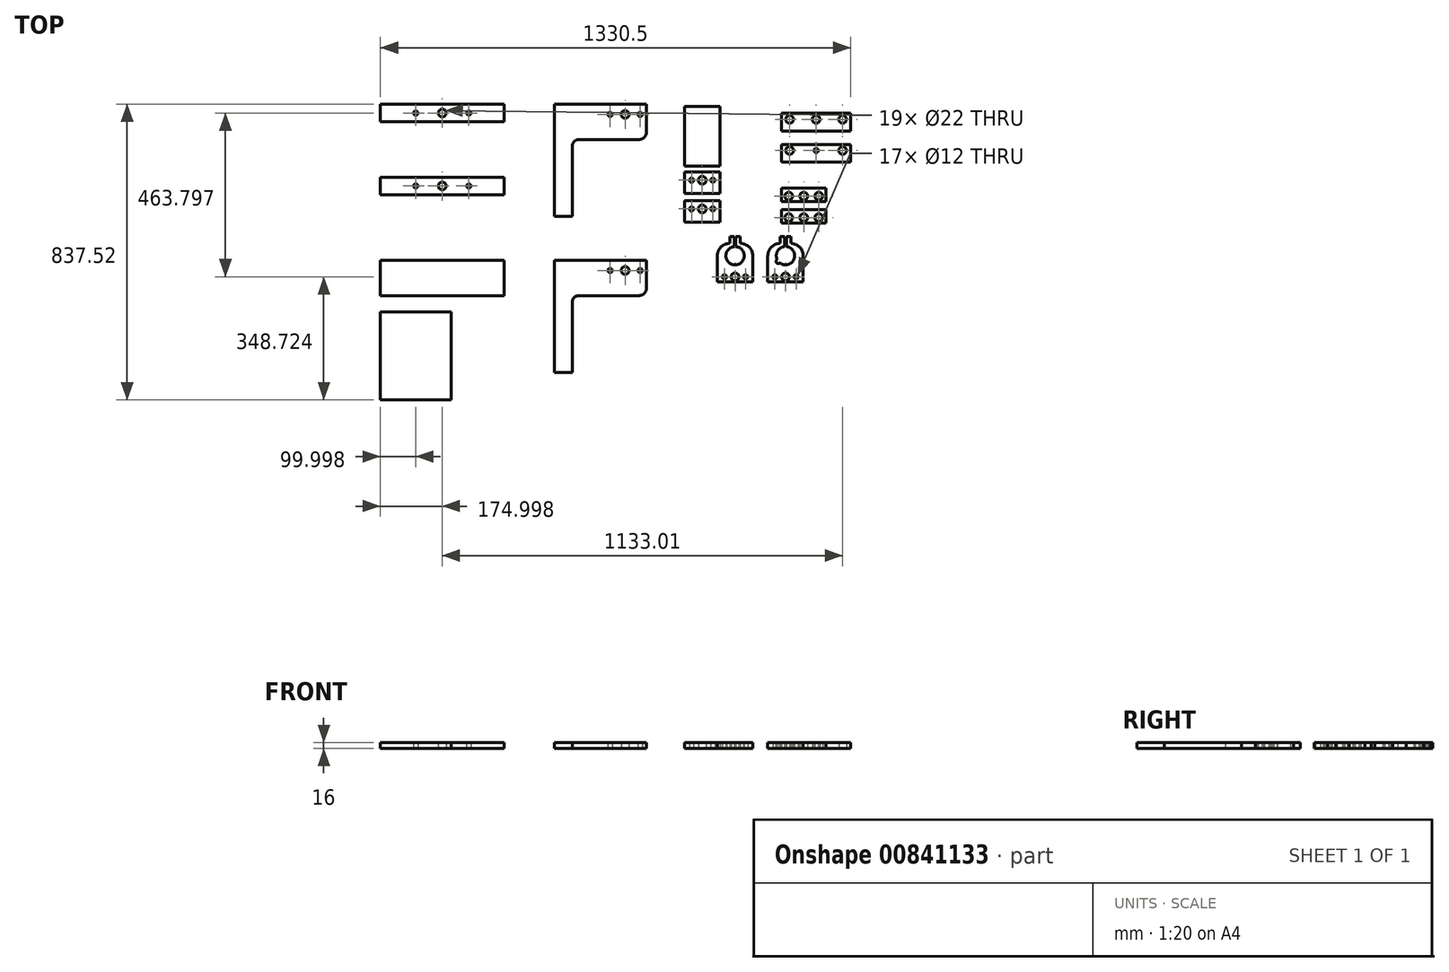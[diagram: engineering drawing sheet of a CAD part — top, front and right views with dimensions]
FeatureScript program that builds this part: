
annotation { "Feature Type Name" : "Feature", "Feature Type Description" : "" }
export const myFeature = defineFeature(function(context is Context, id is Id, definition is map)
    precondition{}
    {
        {
            var Q0;
            Q0=qCreatedBy(makeId("Top.planeOp"),FACE);
            var sketch = newSketch(context, id + "F0", { "sketchPlane" : qUnion([Q0])});
            skLineSegment(sketch, "E0.bottom", {"start": v(-793.1, 335.3) * mm, "end": v(-443.1, 335.3) * mm});
            skLineSegment(sketch, "E0.top", {"start": v(-793.1, 285.3) * mm, "end": v(-443.1, 285.3) * mm});
            skLineSegment(sketch, "E0.left", {"start": v(-793.1, 335.3) * mm, "end": v(-793.1, 285.3) * mm});
            skLineSegment(sketch, "E0.right", {"start": v(-443.1, 335.3) * mm, "end": v(-443.1, 285.3) * mm});
            skLineSegment(sketch, "E1.bottom", {"start": v(-793.1, 100) * mm, "end": v(-443.1, 100) * mm});
            skLineSegment(sketch, "E1.top", {"start": v(-793.1, 0) * mm, "end": v(-443.1, 0) * mm});
            skLineSegment(sketch, "E1.left", {"start": v(-793.1, 100) * mm, "end": v(-793.1, 0) * mm});
            skLineSegment(sketch, "E1.right", {"start": v(-443.1, 100) * mm, "end": v(-443.1, 0) * mm});
            skLineSegment(sketch, "E2", {"start": v(-300.58, 541.75) * mm, "end": v(-40.58, 541.75) * mm});
            skLineSegment(sketch, "E3", {"start": v(-40.58, 541.75) * mm, "end": v(-40.58, 461.75) * mm});
            skLineSegment(sketch, "E4", {"start": v(-60.58, 441.75) * mm, "end": v(-230.58, 441.75) * mm});
            skLineSegment(sketch, "E5", {"start": v(-250.58, 421.75) * mm, "end": v(-250.58, 223.75) * mm});
            skLineSegment(sketch, "E6", {"start": v(-250.58, 223.75) * mm, "end": v(-300.58, 223.75) * mm});
            skLineSegment(sketch, "E7", {"start": v(-300.58, 223.75) * mm, "end": v(-300.58, 541.75) * mm});
            skCircle(sketch, "E8", {"center": v(-693.1, 310.3) * mm, "radius": 6 * mm});
            skCircle(sketch, "E9", {"center": v(-543.1, 310.3) * mm, "radius": 6 * mm});
            skLineSegment(sketch, "E10", {"start": v(-793.1, 310.3) * mm, "end": v(-443.1, 310.3) * mm, "construction": true});
            skCircle(sketch, "E11", {"center": v(-618.1, 310.3) * mm, "radius": 11 * mm});
            skLineSegment(sketch, "E12.bottom", {"start": v(-793.1, 541.75) * mm, "end": v(-443.1, 541.75) * mm});
            skLineSegment(sketch, "E12.top", {"start": v(-793.1, 491.75) * mm, "end": v(-443.1, 491.75) * mm});
            skLineSegment(sketch, "E12.left", {"start": v(-793.1, 541.75) * mm, "end": v(-793.1, 491.75) * mm});
            skLineSegment(sketch, "E12.right", {"start": v(-443.1, 541.75) * mm, "end": v(-443.1, 491.75) * mm});
            skLineSegment(sketch, "E13", {"start": v(-793.1, 516.75) * mm, "end": v(-443.1, 516.75) * mm, "construction": true});
            skCircle(sketch, "E14", {"center": v(-693.1, 516.75) * mm, "radius": 6 * mm});
            skCircle(sketch, "E15", {"center": v(-543.1, 516.75) * mm, "radius": 6 * mm});
            skCircle(sketch, "E16", {"center": v(-618.1, 516.75) * mm, "radius": 11 * mm});
            skLineSegment(sketch, "E17", {"start": v(-300.58, 100) * mm, "end": v(-40.58, 100) * mm});
            skLineSegment(sketch, "E18", {"start": v(-40.58, 100) * mm, "end": v(-40.58, 20) * mm});
            skLineSegment(sketch, "E19", {"start": v(-60.58, 0) * mm, "end": v(-230.58, 0) * mm});
            skLineSegment(sketch, "E20", {"start": v(-250.58, -20) * mm, "end": v(-250.58, -218) * mm});
            skLineSegment(sketch, "E21", {"start": v(-250.58, -218) * mm, "end": v(-300.58, -218) * mm});
            skLineSegment(sketch, "E22", {"start": v(-300.58, -218) * mm, "end": v(-300.58, 100) * mm});
            skLineSegment(sketch, "E23", {"start": v(-40.58, 512.75) * mm, "end": v(-300.58, 512.75) * mm, "construction": true});
            skLineSegment(sketch, "E24", {"start": v(-40.58, 71) * mm, "end": v(-300.58, 71) * mm, "construction": true});
            skCircle(sketch, "E25", {"center": v(-58.15, 512.75) * mm, "radius": 6 * mm});
            skCircle(sketch, "E26", {"center": v(-143.15, 512.75) * mm, "radius": 6 * mm});
            skCircle(sketch, "E27", {"center": v(-58.15, 71) * mm, "radius": 6 * mm});
            skCircle(sketch, "E28", {"center": v(-143.15, 71) * mm, "radius": 6 * mm});
            skCircle(sketch, "E29", {"center": v(-100.58, 512.75) * mm, "radius": 11 * mm});
            skCircle(sketch, "E30", {"center": v(-100.58, 71) * mm, "radius": 11 * mm});
            skPoint(sketch, "E31.visualSharp", {"position": v(-40.58, 441.75) * mm});
            skArc(sketch, "E31.filletArc", {"start": v(-60.58, 441.75) * mm, "mid": v(-46.44, 447.6) * mm, "end": v(-40.58, 461.75) * mm});
            skPoint(sketch, "E32.visualSharp", {"position": v(-250.58, 441.75) * mm});
            skArc(sketch, "E32.filletArc", {"start": v(-230.58, 441.75) * mm, "mid": v(-244.73, 435.9) * mm, "end": v(-250.58, 421.75) * mm});
            skPoint(sketch, "E33.visualSharp", {"position": v(-40.58, 0) * mm});
            skArc(sketch, "E33.filletArc", {"start": v(-60.58, 0) * mm, "mid": v(-46.44, 5.86) * mm, "end": v(-40.58, 20) * mm});
            skPoint(sketch, "E34.visualSharp", {"position": v(-250.58, 0) * mm});
            skArc(sketch, "E34.filletArc", {"start": v(-230.58, 0) * mm, "mid": v(-244.73, -5.86) * mm, "end": v(-250.58, -20) * mm});
            skLineSegment(sketch, "E35.bottom", {"start": v(-793.1, -45.77) * mm, "end": v(-593.1, -45.77) * mm});
            skLineSegment(sketch, "E35.top", {"start": v(-793.1, -295.77) * mm, "end": v(-593.1, -295.77) * mm});
            skLineSegment(sketch, "E35.left", {"start": v(-793.1, -45.77) * mm, "end": v(-793.1, -295.77) * mm});
            skLineSegment(sketch, "E35.right", {"start": v(-593.1, -45.77) * mm, "end": v(-593.1, -295.77) * mm});
            skLineSegment(sketch, "E36.bottom", {"start": v(67.56, 535) * mm, "end": v(167.56, 535) * mm});
            skLineSegment(sketch, "E36.top", {"start": v(67.56, 367) * mm, "end": v(167.56, 367) * mm});
            skLineSegment(sketch, "E36.left", {"start": v(67.56, 535) * mm, "end": v(67.56, 367) * mm});
            skLineSegment(sketch, "E36.right", {"start": v(167.56, 535) * mm, "end": v(167.56, 367) * mm});
            skLineSegment(sketch, "E37.bottom", {"start": v(67.56, 349.5) * mm, "end": v(167.56, 349.5) * mm});
            skLineSegment(sketch, "E37.top", {"start": v(67.56, 289.5) * mm, "end": v(167.56, 289.5) * mm});
            skLineSegment(sketch, "E37.left", {"start": v(67.56, 349.5) * mm, "end": v(67.56, 289.5) * mm});
            skLineSegment(sketch, "E37.right", {"start": v(167.56, 349.5) * mm, "end": v(167.56, 289.5) * mm});
            skPoint(sketch, "E38.oppositeSnap0", {"position": v(167.56, 319.5) * mm});
            skLineSegment(sketch, "E39.bottom", {"start": v(342.4, 515.9) * mm, "end": v(537.4, 515.9) * mm});
            skLineSegment(sketch, "E39.top", {"start": v(342.4, 465.9) * mm, "end": v(537.4, 465.9) * mm});
            skLineSegment(sketch, "E39.left", {"start": v(342.4, 515.9) * mm, "end": v(342.4, 465.9) * mm});
            skLineSegment(sketch, "E39.right", {"start": v(537.4, 515.9) * mm, "end": v(537.4, 465.9) * mm});
            skLineSegment(sketch, "E40", {"start": v(67.56, 326.5) * mm, "end": v(167.56, 326.5) * mm, "construction": true});
            skCircle(sketch, "E41", {"center": v(117.56, 326.5) * mm, "radius": 11 * mm});
            skCircle(sketch, "E42", {"center": v(87.56, 326.5) * mm, "radius": 6 * mm});
            skCircle(sketch, "E43", {"center": v(147.56, 326.5) * mm, "radius": 6 * mm});
            skLineSegment(sketch, "E44.bottom", {"start": v(67.56, 268.28) * mm, "end": v(167.56, 268.28) * mm});
            skLineSegment(sketch, "E44.top", {"start": v(67.56, 208.28) * mm, "end": v(167.56, 208.28) * mm});
            skLineSegment(sketch, "E44.left", {"start": v(67.56, 268.28) * mm, "end": v(67.56, 208.28) * mm});
            skLineSegment(sketch, "E44.right", {"start": v(167.56, 268.28) * mm, "end": v(167.56, 208.28) * mm});
            skPoint(sketch, "E45.oppositeSnap0", {"position": v(167.56, 238.28) * mm});
            skLineSegment(sketch, "E46", {"start": v(67.56, 245.28) * mm, "end": v(167.56, 245.28) * mm, "construction": true});
            skCircle(sketch, "E47", {"center": v(117.56, 245.28) * mm, "radius": 11 * mm});
            skCircle(sketch, "E48", {"center": v(87.56, 245.28) * mm, "radius": 6 * mm});
            skCircle(sketch, "E49", {"center": v(147.56, 245.28) * mm, "radius": 6 * mm});
            skLineSegment(sketch, "E50", {"start": v(342.4, 498.9) * mm, "end": v(537.4, 498.9) * mm, "construction": true});
            skCircle(sketch, "E51", {"center": v(364.9, 498.9) * mm, "radius": 11 * mm});
            skCircle(sketch, "E52", {"center": v(514.9, 498.9) * mm, "radius": 11 * mm});
            skCircle(sketch, "E53", {"center": v(439.9, 498.9) * mm, "radius": 11 * mm});
            skLineSegment(sketch, "E54.bottom", {"start": v(342.4, 427.64) * mm, "end": v(537.4, 427.64) * mm});
            skLineSegment(sketch, "E54.top", {"start": v(342.4, 377.64) * mm, "end": v(537.4, 377.64) * mm});
            skLineSegment(sketch, "E54.left", {"start": v(342.4, 427.64) * mm, "end": v(342.4, 377.64) * mm});
            skLineSegment(sketch, "E54.right", {"start": v(537.4, 427.64) * mm, "end": v(537.4, 377.64) * mm});
            skLineSegment(sketch, "E55", {"start": v(342.4, 410.64) * mm, "end": v(537.4, 410.64) * mm, "construction": true});
            skCircle(sketch, "E56", {"center": v(364.9, 410.64) * mm, "radius": 11 * mm});
            skCircle(sketch, "E57", {"center": v(514.9, 410.64) * mm, "radius": 11 * mm});
            skCircle(sketch, "E58", {"center": v(439.9, 410.64) * mm, "radius": 6 * mm});
            skLineSegment(sketch, "E59.bottom", {"start": v(342.4, 304.54) * mm, "end": v(467.4, 304.54) * mm});
            skLineSegment(sketch, "E59.top", {"start": v(342.4, 266.54) * mm, "end": v(467.4, 266.54) * mm});
            skLineSegment(sketch, "E59.left", {"start": v(342.4, 304.54) * mm, "end": v(342.4, 266.54) * mm});
            skLineSegment(sketch, "E59.right", {"start": v(467.4, 304.54) * mm, "end": v(467.4, 266.54) * mm});
            skPoint(sketch, "E60.oppositeSnap0", {"position": v(467.4, 285.54) * mm});
            skLineSegment(sketch, "E61", {"start": v(342.4, 281.54) * mm, "end": v(467.4, 281.54) * mm, "construction": true});
            skCircle(sketch, "E62", {"center": v(404.9, 281.54) * mm, "radius": 11 * mm});
            skCircle(sketch, "E63", {"center": v(362.4, 281.54) * mm, "radius": 11 * mm});
            skCircle(sketch, "E64", {"center": v(447.4, 281.54) * mm, "radius": 11 * mm});
            skLineSegment(sketch, "E65.bottom", {"start": v(342.4, 243.72) * mm, "end": v(467.4, 243.72) * mm});
            skLineSegment(sketch, "E65.top", {"start": v(342.4, 205.72) * mm, "end": v(467.4, 205.72) * mm});
            skLineSegment(sketch, "E65.left", {"start": v(342.4, 243.72) * mm, "end": v(342.4, 205.72) * mm});
            skLineSegment(sketch, "E65.right", {"start": v(467.4, 243.72) * mm, "end": v(467.4, 205.72) * mm});
            skPoint(sketch, "E66.oppositeSnap0", {"position": v(467.4, 224.72) * mm});
            skLineSegment(sketch, "E67", {"start": v(342.4, 220.72) * mm, "end": v(467.4, 220.72) * mm, "construction": true});
            skCircle(sketch, "E68", {"center": v(404.9, 220.72) * mm, "radius": 11 * mm});
            skCircle(sketch, "E69", {"center": v(362.4, 220.72) * mm, "radius": 11 * mm});
            skCircle(sketch, "E70", {"center": v(447.4, 220.72) * mm, "radius": 11 * mm});
            skLineSegment(sketch, "E71.bottom", {"start": v(160.46, 78.95) * mm, "end": v(260.46, 78.95) * mm});
            skLineSegment(sketch, "E71.top", {"start": v(160.46, 38.95) * mm, "end": v(260.46, 38.95) * mm});
            skLineSegment(sketch, "E71.left", {"start": v(160.46, 78.95) * mm, "end": v(160.46, 38.95) * mm});
            skLineSegment(sketch, "E71.right", {"start": v(260.46, 78.95) * mm, "end": v(260.46, 38.95) * mm});
            skPoint(sketch, "E72.oppositeSnap0", {"position": v(260.46, 58.95) * mm});
            skLineSegment(sketch, "E73", {"start": v(160.46, 52.95) * mm, "end": v(260.46, 52.95) * mm, "construction": true});
            skCircle(sketch, "E74", {"center": v(210.46, 52.95) * mm, "radius": 11 * mm});
            skCircle(sketch, "E75", {"center": v(180.46, 52.95) * mm, "radius": 6 * mm});
            skCircle(sketch, "E76", {"center": v(240.46, 52.95) * mm, "radius": 6 * mm});
            skCircle(sketch, "E77", {"center": v(210.46, 112.78) * mm, "radius": 26 * mm});
            skPoint(sketch, "E77.centerSnap0", {"position": v(210.46, 78.95) * mm});
            skLineSegment(sketch, "E78.left", {"start": v(160.46, 78.95) * mm, "end": v(160.46, 112.63) * mm});
            skLineSegment(sketch, "E78.right", {"start": v(260.46, 78.95) * mm, "end": v(260.46, 112.63) * mm});
            skPoint(sketch, "E79.visualSharp", {"position": v(160.46, 147.63) * mm});
            skArc(sketch, "E79.filletArc", {"start": v(195.51, 147.63) * mm, "mid": v(170.73, 137.4) * mm, "end": v(160.46, 112.63) * mm});
            skPoint(sketch, "E80.visualSharp", {"position": v(260.46, 147.63) * mm});
            skArc(sketch, "E80.filletArc", {"start": v(260.46, 112.63) * mm, "mid": v(250.21, 137.38) * mm, "end": v(225.46, 147.63) * mm});
            skLineSegment(sketch, "E81.top", {"start": v(195.51, 166.54) * mm, "end": v(225.46, 166.54) * mm});
            skLineSegment(sketch, "E81.left", {"start": v(195.51, 147.63) * mm, "end": v(195.51, 166.54) * mm});
            skLineSegment(sketch, "E81.right", {"start": v(225.46, 147.63) * mm, "end": v(225.46, 166.54) * mm});
            skPoint(sketch, "E82.oppositeSnap0", {"position": v(210.49, 166.54) * mm});
            skLineSegment(sketch, "E83.bottom", {"start": v(208.9, 166.54) * mm, "end": v(212.07, 166.54) * mm});
            skSolve(sketch);
        }
        {
            var Q0;
            Q0=qSketchRegion(id+"F0",true);
            extrude(context, id + "F1", {"entities" : qUnion([Q0]), "depth" : 16 * mm, "offsetDistance" : 25 * mm});
        }
        {
            var Q0;
            Q0=makeQuery(id+"F1.opExtrude","SWEPT_FACE",FACE,{"disambiguationData":[OSD([sQuery(id+"F0.wireOp",EDGE,"E81.top"),sQuery(id+"F0.wireOp",EDGE,"E83.bottom")])]});
            var sketch = newSketch(context, id + "F2", { "sketchPlane" : qUnion([Q0])});
            skLineSegment(sketch, "E84.bottom", {"start": v(-208.34, 17.1) * mm, "end": v(-212.64, 17.1) * mm});
            skLineSegment(sketch, "E84.top", {"start": v(-208.34, -17.1) * mm, "end": v(-212.64, -17.1) * mm});
            skLineSegment(sketch, "E84.left", {"start": v(-208.34, 17.1) * mm, "end": v(-208.34, -17.1) * mm});
            skLineSegment(sketch, "E84.right", {"start": v(-212.64, 17.1) * mm, "end": v(-212.64, -17.1) * mm});
            skPoint(sketch, "E84.middle", {"position": v(-210.49, 0) * mm});
            skSolve(sketch);
        }
        {
            var Q0;
            Q0=qSketchRegion(id+"F2",true);
            extrude(context, id + "F3", {"entities" : qUnion([Q0]), "operationType" : NewBodyOperationType.REMOVE, "oppositeDirection" : true, "depth" : 51 * mm, "offsetDistance" : 25 * mm});
        }
        {
            var Q0;
            Q0=makeQuery(id+"F1.opExtrude","SWEPT_BODY",BODY,{"disambiguationData":[OSD([sQuery(id+"F0.wireOp",EDGE,"E71.top"),sQuery(id+"F0.wireOp",EDGE,"E71.left"),sQuery(id+"F0.wireOp",EDGE,"E71.right"),sQuery(id+"F0.wireOp",EDGE,"E74"),sQuery(id+"F0.wireOp",EDGE,"E75"),sQuery(id+"F0.wireOp",EDGE,"E76"),sQuery(id+"F0.wireOp",EDGE,"E77"),sQuery(id+"F0.wireOp",EDGE,"E78.left"),sQuery(id+"F0.wireOp",EDGE,"E78.right"),sQuery(id+"F0.wireOp",EDGE,"E79.filletArc"),sQuery(id+"F0.wireOp",EDGE,"E80.filletArc"),sQuery(id+"F0.wireOp",EDGE,"E81.top"),sQuery(id+"F0.wireOp",EDGE,"E81.left"),sQuery(id+"F0.wireOp",EDGE,"E81.right"),sQuery(id+"F0.wireOp",EDGE,"E83.bottom")])]});
            transform(context, id + "F4", {"entities" : qUnion([Q0]), "transformType" : TransformType.COPY});
        }
        {
            var Q0;
            Q0=makeQuery(id+"F4.opPattern","COPY",BODY,{"derivedFrom":makeQuery(id+"F1.opExtrude","SWEPT_BODY",BODY,{"disambiguationData":[OSD([sQuery(id+"F0.wireOp",EDGE,"E71.top"),sQuery(id+"F0.wireOp",EDGE,"E71.left"),sQuery(id+"F0.wireOp",EDGE,"E71.right"),sQuery(id+"F0.wireOp",EDGE,"E74"),sQuery(id+"F0.wireOp",EDGE,"E75"),sQuery(id+"F0.wireOp",EDGE,"E76"),sQuery(id+"F0.wireOp",EDGE,"E77"),sQuery(id+"F0.wireOp",EDGE,"E78.left"),sQuery(id+"F0.wireOp",EDGE,"E78.right"),sQuery(id+"F0.wireOp",EDGE,"E79.filletArc"),sQuery(id+"F0.wireOp",EDGE,"E80.filletArc"),sQuery(id+"F0.wireOp",EDGE,"E81.top"),sQuery(id+"F0.wireOp",EDGE,"E81.left"),sQuery(id+"F0.wireOp",EDGE,"E81.right"),sQuery(id+"F0.wireOp",EDGE,"E83.bottom")])]}),"instanceName":"1"});
            transform(context, id + "F5", {"entities" : qUnion([Q0]), "transformType" : TransformType.TRANSLATION_3D, "dx" : 142.7 * mm, "dy" : 0 * mm, "dz" : 0 * mm, "makeCopy" : true});
        }
        {
            var Q0;
            Q0=makeQuery(id+"F4.opPattern","COPY",BODY,{"derivedFrom":makeQuery(id+"F1.opExtrude","SWEPT_BODY",BODY,{"disambiguationData":[OSD([sQuery(id+"F0.wireOp",EDGE,"E71.top"),sQuery(id+"F0.wireOp",EDGE,"E71.left"),sQuery(id+"F0.wireOp",EDGE,"E71.right"),sQuery(id+"F0.wireOp",EDGE,"E74"),sQuery(id+"F0.wireOp",EDGE,"E75"),sQuery(id+"F0.wireOp",EDGE,"E76"),sQuery(id+"F0.wireOp",EDGE,"E77"),sQuery(id+"F0.wireOp",EDGE,"E78.left"),sQuery(id+"F0.wireOp",EDGE,"E78.right"),sQuery(id+"F0.wireOp",EDGE,"E79.filletArc"),sQuery(id+"F0.wireOp",EDGE,"E80.filletArc"),sQuery(id+"F0.wireOp",EDGE,"E81.top"),sQuery(id+"F0.wireOp",EDGE,"E81.left"),sQuery(id+"F0.wireOp",EDGE,"E81.right"),sQuery(id+"F0.wireOp",EDGE,"E83.bottom")])]}),"instanceName":"1"});
            deleteBodies(context, id + "F6", {"entities" : qUnion([Q0])});
        }
        {
            var Q0;
            Q0=makeQuery(id+"F5.opPattern","COPY",FACE,{"derivedFrom":makeQuery(id+"F4.opPattern","COPY",FACE,{"derivedFrom":makeQuery(id+"F1.opExtrude","CAP_FACE",FACE,{"disambiguationData":[OSD([sQuery(id+"F0.wireOp",EDGE,"E71.top"),sQuery(id+"F0.wireOp",EDGE,"E71.left"),sQuery(id+"F0.wireOp",EDGE,"E71.right"),sQuery(id+"F0.wireOp",EDGE,"E74"),sQuery(id+"F0.wireOp",EDGE,"E75"),sQuery(id+"F0.wireOp",EDGE,"E76"),sQuery(id+"F0.wireOp",EDGE,"E77"),sQuery(id+"F0.wireOp",EDGE,"E78.left"),sQuery(id+"F0.wireOp",EDGE,"E78.right"),sQuery(id+"F0.wireOp",EDGE,"E79.filletArc"),sQuery(id+"F0.wireOp",EDGE,"E80.filletArc"),sQuery(id+"F0.wireOp",EDGE,"E81.top"),sQuery(id+"F0.wireOp",EDGE,"E81.left"),sQuery(id+"F0.wireOp",EDGE,"E81.right"),sQuery(id+"F0.wireOp",EDGE,"E83.bottom")])],"isStart":false}),"instanceName":"1"}),"instanceName":"1"});
            var sketch = newSketch(context, id + "F7", { "sketchPlane" : qUnion([Q0])});
            skCircle(sketch, "E85", {"center": v(332.58, 96.9) * mm, "radius": 6.4 * mm});
            skSolve(sketch);
        }
        {
            var Q0;
            Q0=qSketchRegion(id+"F7",true);
            extrude(context, id + "F8", {"entities" : qUnion([Q0]), "operationType" : NewBodyOperationType.REMOVE, "endBound" : BoundingType.THROUGH_ALL, "oppositeDirection" : true, "depth" : 25 * mm, "offsetDistance" : 25 * mm});
        }
    });
